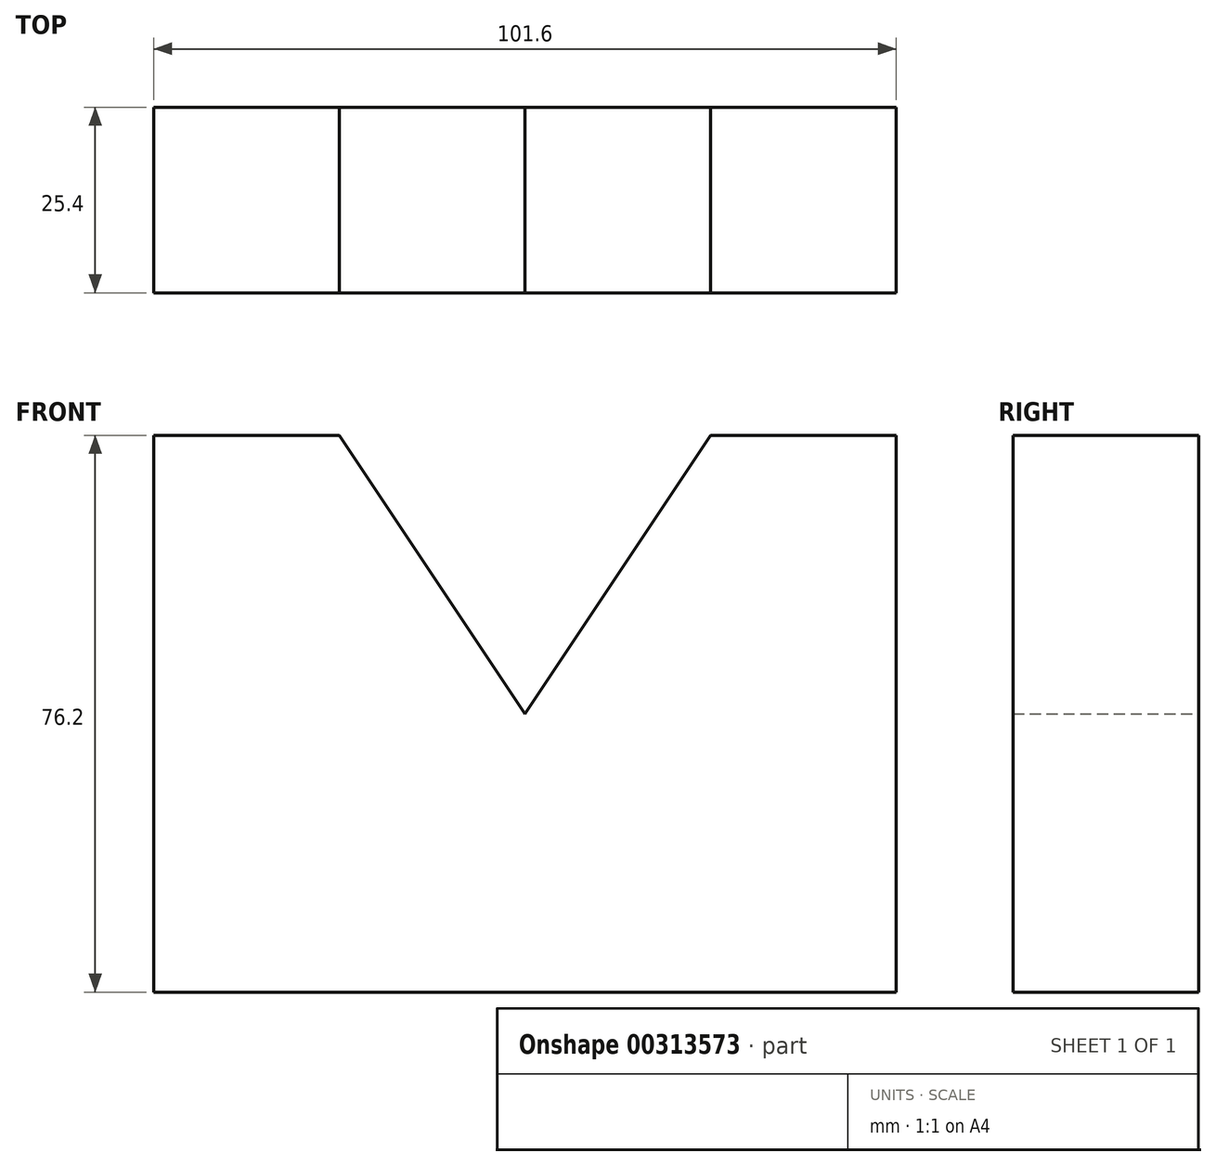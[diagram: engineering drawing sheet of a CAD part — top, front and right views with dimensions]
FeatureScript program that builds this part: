
annotation { "Feature Type Name" : "Feature", "Feature Type Description" : "" }
export const myFeature = defineFeature(function(context is Context, id is Id, definition is map)
    precondition{}
    {
        {
            var Q0;
            Q0=qCreatedBy(makeId("Front.planeOp"),FACE);
            var sketch = newSketch(context, id + "F0", { "sketchPlane" : qUnion([Q0])});
            skLineSegment(sketch, "E0", {"start": v(-25.4, 38.1) * mm, "end": v(-50.8, 38.1) * mm});
            skLineSegment(sketch, "E1", {"start": v(-50.8, 38.1) * mm, "end": v(-50.8, -38.1) * mm});
            skLineSegment(sketch, "E2", {"start": v(-50.8, -38.1) * mm, "end": v(50.8, -38.1) * mm});
            skLineSegment(sketch, "E3", {"start": v(50.8, -38.1) * mm, "end": v(50.8, 38.1) * mm});
            skLineSegment(sketch, "E4", {"start": v(50.8, 38.1) * mm, "end": v(25.4, 38.1) * mm});
            skLineSegment(sketch, "E5", {"start": v(25.4, 38.1) * mm, "end": v(0, 0) * mm});
            skLineSegment(sketch, "E6", {"start": v(0, 0) * mm, "end": v(-25.4, 38.1) * mm});
            skSolve(sketch);
        }
        {
            var Q0;
            Q0=makeQuery(id+"F0.imprint","IMPRINT",FACE,{"disambiguationData":[TD([[makeQuery(id+"F0.imprint","IMPRINT",EDGE,{"derivedFrom":sQuery(id+"F0.wireOp",EDGE,"E0")}),1.0]])]});
            extrude(context, id + "F1", {"entities" : qUnion([Q0]), "depth" : 25.4 * mm});
        }
    });
